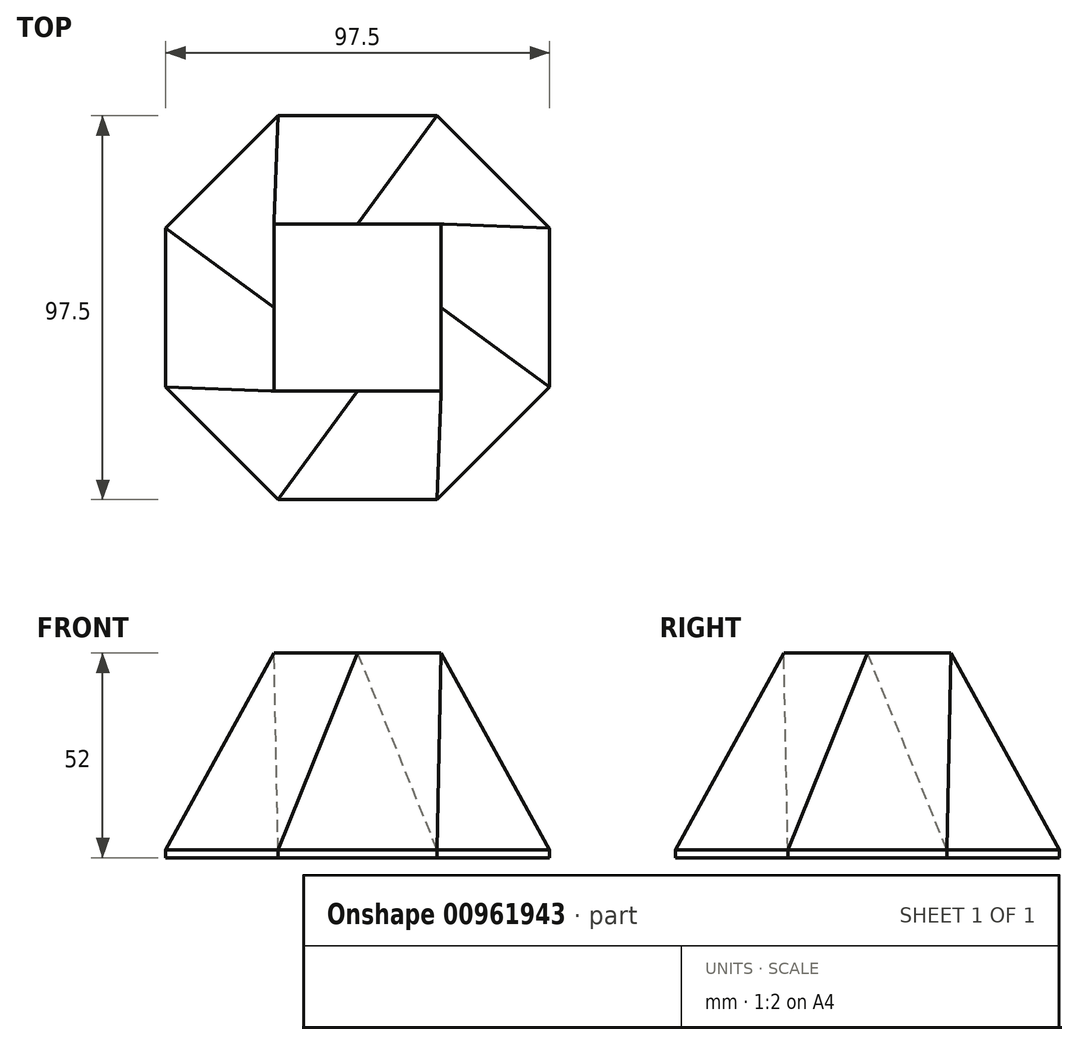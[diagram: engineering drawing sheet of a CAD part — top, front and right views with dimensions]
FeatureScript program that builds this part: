
annotation { "Feature Type Name" : "Feature", "Feature Type Description" : "" }
export const myFeature = defineFeature(function(context is Context, id is Id, definition is map)
    precondition{}
    {
        {
            var Q0;
            Q0=qCreatedBy(makeId("Top.planeOp"),FACE);
            var sketch = newSketch(context, id + "F0", { "sketchPlane" : qUnion([Q0])});
            skCircle(sketch, "E0", {"center": v(0, 0) * mm, "radius": 48.75 * mm});
            skCircle(sketch, "E1.cCircle", {"center": v(0, 0) * mm, "radius": 48.75 * mm, "construction": true});
            skLineSegment(sketch, "E1.0", {"start": v(-48.75, -20.2) * mm, "end": v(-48.75, 20.2) * mm});
            skLineSegment(sketch, "E1.1", {"start": v(-48.75, 20.2) * mm, "end": v(-20.2, 48.75) * mm});
            skLineSegment(sketch, "E1.2", {"start": v(-20.2, 48.75) * mm, "end": v(20.2, 48.75) * mm});
            skLineSegment(sketch, "E1.3", {"start": v(20.2, 48.75) * mm, "end": v(48.75, 20.2) * mm});
            skLineSegment(sketch, "E1.4", {"start": v(48.75, 20.2) * mm, "end": v(48.75, -20.2) * mm});
            skLineSegment(sketch, "E1.5", {"start": v(48.75, -20.2) * mm, "end": v(20.2, -48.75) * mm});
            skLineSegment(sketch, "E1.6", {"start": v(20.2, -48.75) * mm, "end": v(-20.2, -48.75) * mm});
            skLineSegment(sketch, "E1.7", {"start": v(-20.2, -48.75) * mm, "end": v(-48.75, -20.2) * mm});
            skPoint(sketch, "E1.0.midPoint", {"position": v(-48.75, 0) * mm});
            skSolve(sketch);
        }
        {
            var Q0;
            Q0=qSketchRegion(id+"F0",true);
            extrude(context, id + "F1", {"entities" : qUnion([Q0]), "depth" : 2 * mm, "offsetDistance" : 25 * mm});
        }
        {
            var Q0;
            Q0=makeQuery(id+"F1.opExtrude","CAP_FACE",FACE,{"disambiguationData":[OSD([sQuery(id+"F0.wireOp",EDGE,"E1.0"),sQuery(id+"F0.wireOp",EDGE,"E1.1"),sQuery(id+"F0.wireOp",EDGE,"E1.2"),sQuery(id+"F0.wireOp",EDGE,"E1.3"),sQuery(id+"F0.wireOp",EDGE,"E1.4"),sQuery(id+"F0.wireOp",EDGE,"E1.5"),sQuery(id+"F0.wireOp",EDGE,"E1.6"),sQuery(id+"F0.wireOp",EDGE,"E1.7")])],"isStart":false});
            cPlane(context, id + "F2", {"entities" : qUnion([Q0]), "cplaneType" : CPlaneType.OFFSET, "offset" : 50 * mm, "width" : 150 * mm, "height" : 150 * mm});
        }
        {
            var Q0;
            Q0=qCreatedBy(id+"F2.planeOp",FACE);
            var sketch = newSketch(context, id + "F3", { "sketchPlane" : qUnion([Q0])});
            skLineSegment(sketch, "E2.1", {"start": v(-30, 12.43) * mm, "end": v(-12.43, 30) * mm});
            skLineSegment(sketch, "E2.3", {"start": v(12.43, 30) * mm, "end": v(30, 12.43) * mm});
            skLineSegment(sketch, "E2.5", {"start": v(30, -12.43) * mm, "end": v(12.43, -30) * mm});
            skLineSegment(sketch, "E2.7", {"start": v(-12.43, -30) * mm, "end": v(-30, -12.43) * mm});
            skPoint(sketch, "E2.0.midPoint", {"position": v(-30, 0) * mm});
            skLineSegment(sketch, "E3.bottom", {"start": v(-21.21, 21.21) * mm, "end": v(21.21, 21.21) * mm});
            skLineSegment(sketch, "E3.top", {"start": v(-21.21, -21.21) * mm, "end": v(21.21, -21.21) * mm});
            skLineSegment(sketch, "E3.left", {"start": v(-21.21, 21.21) * mm, "end": v(-21.21, -21.21) * mm});
            skLineSegment(sketch, "E3.right", {"start": v(21.21, 21.21) * mm, "end": v(21.21, -21.21) * mm});
            skPoint(sketch, "E3.middle", {"position": v(0, 0) * mm});
            skSolve(sketch);
        }
        {
            var Q0;
            Q0=makeQuery(id+"F1.opExtrude","CAP_FACE",FACE,{"disambiguationData":[OSD([sQuery(id+"F0.wireOp",EDGE,"E1.0"),sQuery(id+"F0.wireOp",EDGE,"E1.1"),sQuery(id+"F0.wireOp",EDGE,"E1.2"),sQuery(id+"F0.wireOp",EDGE,"E1.3"),sQuery(id+"F0.wireOp",EDGE,"E1.4"),sQuery(id+"F0.wireOp",EDGE,"E1.5"),sQuery(id+"F0.wireOp",EDGE,"E1.6"),sQuery(id+"F0.wireOp",EDGE,"E1.7")])],"isStart":false});
            var sketch = newSketch(context, id + "F4", { "sketchPlane" : qUnion([Q0])});
            skCircle(sketch, "E4.cCircle", {"center": v(0, 0) * mm, "radius": 48.75 * mm, "construction": true});
            skLineSegment(sketch, "E4.0", {"start": v(-48.75, -20.2) * mm, "end": v(-48.75, 20.2) * mm});
            skLineSegment(sketch, "E4.1", {"start": v(-48.75, 20.2) * mm, "end": v(-20.2, 48.75) * mm});
            skLineSegment(sketch, "E4.2", {"start": v(-20.2, 48.75) * mm, "end": v(20.2, 48.75) * mm});
            skLineSegment(sketch, "E4.3", {"start": v(20.2, 48.75) * mm, "end": v(48.75, 20.2) * mm});
            skLineSegment(sketch, "E4.4", {"start": v(48.75, 20.2) * mm, "end": v(48.75, -20.2) * mm});
            skLineSegment(sketch, "E4.5", {"start": v(48.75, -20.2) * mm, "end": v(20.2, -48.75) * mm});
            skLineSegment(sketch, "E4.6", {"start": v(20.2, -48.75) * mm, "end": v(-20.2, -48.75) * mm});
            skLineSegment(sketch, "E4.7", {"start": v(-20.2, -48.75) * mm, "end": v(-48.75, -20.2) * mm});
            skPoint(sketch, "E4.0.midPoint", {"position": v(-48.75, 0) * mm});
            skSolve(sketch);
        }
        {
            var Q1;
            Q1=qSketchRegion(id+"F4",true);
            var Q2;
            Q2 = qSketchRegion(id + "F3", true);
            var Q3;
            Q3=sQuery(id+"F4.wireOp",VERTEX,"E4.3.end");
            var Q4;
            Q4=sQuery(id+"F3.wireOp",VERTEX,"E3.bottom.end");
            loft(context, id + "F5", {"operationType" : NewBodyOperationType.ADD, "sheetProfilesArray" : [{ "sheetProfileEntities" : qUnion([Q1]) }, { "sheetProfileEntities" : qUnion([Q2]) }], "matchConnections" : true, "connections" : [{ "connectionEntities" : qUnion([Q3, Q4]), "connectionEdgeQueries" : qUnion([]), "connectionEdgeParameters" : [] }]});
        }
    });
